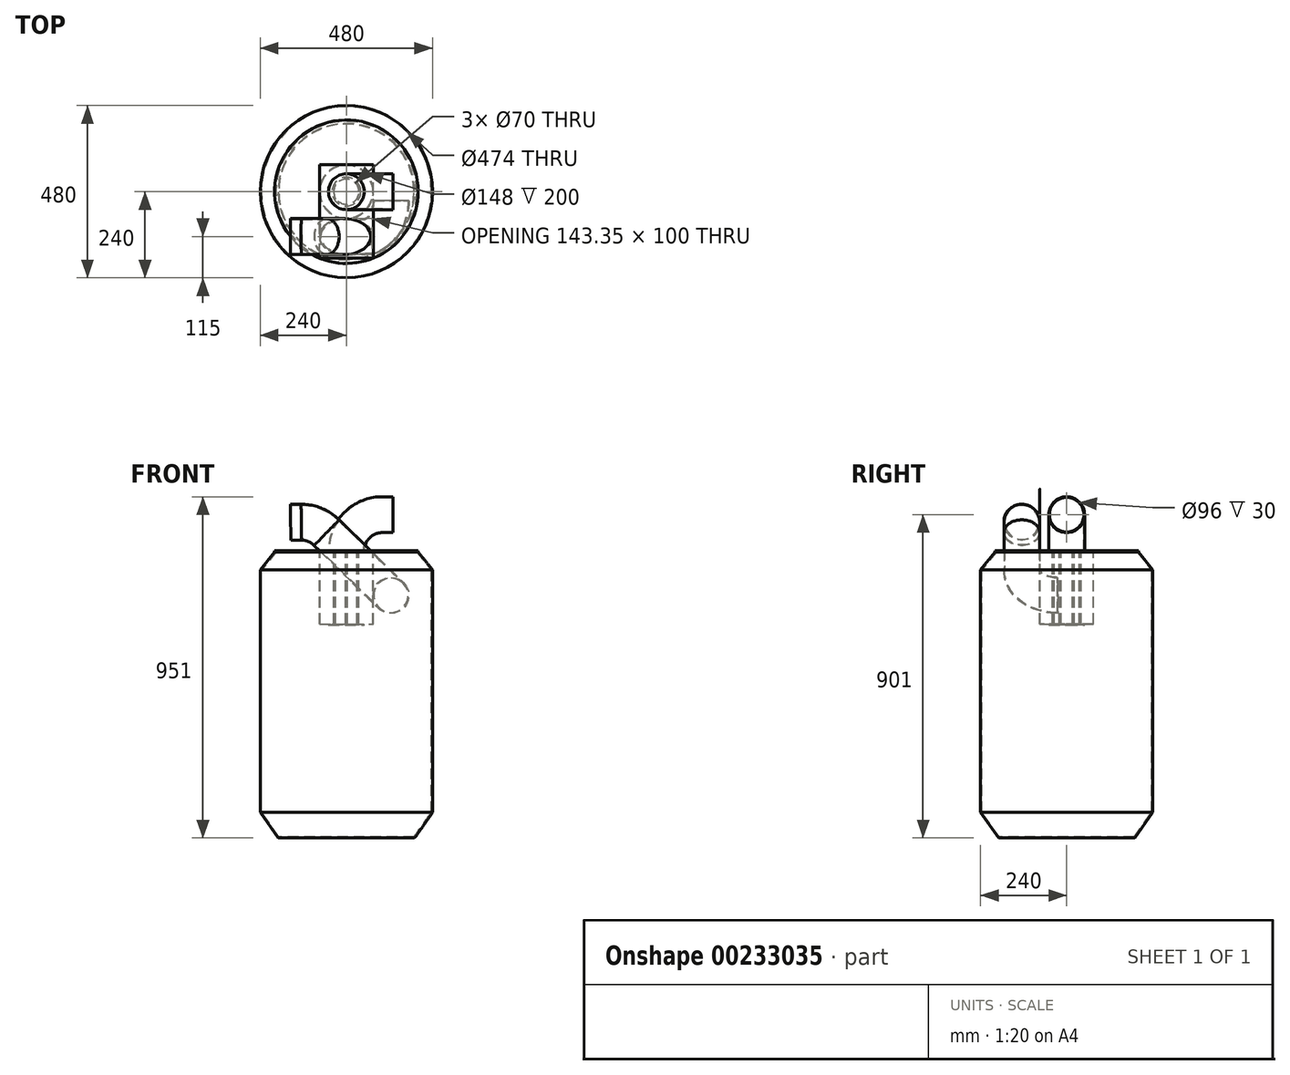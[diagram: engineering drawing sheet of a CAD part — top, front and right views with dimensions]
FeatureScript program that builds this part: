
annotation { "Feature Type Name" : "Feature", "Feature Type Description" : "" }
export const myFeature = defineFeature(function(context is Context, id is Id, definition is map)
    precondition{}
    {
        {
            assignVariable(context, id + "F0", {"name" : "FilterHeight", "anyValue" : 200});
        }
        {
            var Q0;
            Q0=qCreatedBy(makeId("Top.planeOp"),FACE);
            var sketch = newSketch(context, id + "F1", { "sketchPlane" : qUnion([Q0])});
            skCircle(sketch, "E0", {"center": v(0, 0) * mm, "radius": 200 * mm});
            skCircle(sketch, "E1", {"center": v(0, 0) * mm, "radius": 35 * mm});
            skSolve(sketch);
        }
        {
            var Q0;
            Q0=qSketchRegion(id+"F1",true);
            extrude(context, id + "F2", {"entities" : qUnion([Q0]), "depth" : 3 * mm});
        }
        {
            var Q0;
            Q0=makeQuery(id+"F2.opExtrude","CAP_FACE",FACE,{"disambiguationData":[OSD([sQuery(id+"F1.wireOp",EDGE,"E0"),sQuery(id+"F1.wireOp",EDGE,"E1")])],"isStart":true});
            var sketch = newSketch(context, id + "F3", { "sketchPlane" : qUnion([Q0])});
            skLineSegment(sketch, "E2.bottom", {"start": v(75, -75) * mm, "end": v(-75, -75) * mm});
            skLineSegment(sketch, "E2.top", {"start": v(75, 75) * mm, "end": v(-75, 75) * mm});
            skLineSegment(sketch, "E2.left", {"start": v(75, -75) * mm, "end": v(75, 75) * mm});
            skLineSegment(sketch, "E2.right", {"start": v(-75, -75) * mm, "end": v(-75, 75) * mm});
            skPoint(sketch, "E2.middle", {"position": v(0, 0) * mm});
            skCircle(sketch, "E3.0", {"center": v(0, 0) * mm, "radius": 35 * mm});
            skLineSegment(sketch, "E4.top", {"start": v(75, 185.4) * mm, "end": v(-75, 185.4) * mm});
            skLineSegment(sketch, "E4.left", {"start": v(75, 75) * mm, "end": v(75, 185.4) * mm});
            skLineSegment(sketch, "E4.right", {"start": v(-75, 75) * mm, "end": v(-75, 185.4) * mm});
            skSolve(sketch);
        }
        {
            var Q0;
            Q0=qSketchRegion(id+"F3",true);
            extrude(context, id + "F4", {"entities" : qUnion([Q0]), "depth" : 1 * mm});
        }
        {
            var Q0;
            Q0=makeQuery(id+"F4.opExtrude","CAP_FACE",FACE,{"disambiguationData":[OSD([sQuery(id+"F3.wireOp",EDGE,"E2.bottom"),sQuery(id+"F3.wireOp",EDGE,"E2.top"),sQuery(id+"F3.wireOp",EDGE,"E2.left"),sQuery(id+"F3.wireOp",EDGE,"E2.right"),sQuery(id+"F3.wireOp",EDGE,"E3.0")])],"isStart":false});
            var sketch = newSketch(context, id + "F5", { "sketchPlane" : qUnion([Q0])});
            skCircle(sketch, "E5", {"center": v(0, 37.5) * mm, "radius": 2.5 * mm});
            skCircle(sketch, "E6.1.0", {"center": v(-32.48, 18.75) * mm, "radius": 2.5 * mm});
            skCircle(sketch, "E6.2.0", {"center": v(-32.48, -18.75) * mm, "radius": 2.5 * mm});
            skCircle(sketch, "E6.3.0", {"center": v(0, -37.5) * mm, "radius": 2.5 * mm});
            skCircle(sketch, "E6.4.0", {"center": v(32.48, -18.75) * mm, "radius": 2.5 * mm});
            skCircle(sketch, "E6.5.0", {"center": v(32.48, 18.75) * mm, "radius": 2.5 * mm});
            skPoint(sketch, "E6.center", {"position": v(0, 0) * mm});
            skSolve(sketch);
        }
        {
            var Q0;
            Q0=qSketchRegion(id+"F5",true);
            extrude(context, id + "F6", {"entities" : qUnion([Q0]), "depth" : (getVariable(context, 'FilterHeight')) * mm});
        }
        {
            var Q0;
            Q0=makeQuery(id+"F6.opExtrude","CAP_FACE",FACE,{"disambiguationData":[OSD([sQuery(id+"F5.wireOp",EDGE,"E5")])],"isStart":false});
            var sketch = newSketch(context, id + "F7", { "sketchPlane" : qUnion([Q0])});
            skCircle(sketch, "E7", {"center": v(0, 0) * mm, "radius": 40 * mm});
            skSolve(sketch);
        }
        {
            var Q0;
            Q0=qSketchRegion(id+"F7",true);
            extrude(context, id + "F8", {"entities" : qUnion([Q0]), "depth" : 1 * mm});
        }
        {
            var Q0;
            Q0=makeQuery(id+"F4.opExtrude","CAP_FACE",FACE,{"disambiguationData":[OSD([sQuery(id+"F3.wireOp",EDGE,"E2.bottom"),sQuery(id+"F3.wireOp",EDGE,"E2.top"),sQuery(id+"F3.wireOp",EDGE,"E2.left"),sQuery(id+"F3.wireOp",EDGE,"E2.right"),sQuery(id+"F3.wireOp",EDGE,"E3.0")])],"isStart":false});
            var sketch = newSketch(context, id + "F9", { "sketchPlane" : qUnion([Q0])});
            skCircle(sketch, "E8", {"center": v(0, 0) * mm, "radius": 75 * mm});
            skCircle(sketch, "E9.0", {"center": v(0, 0) * mm, "radius": 74 * mm});
            skSolve(sketch);
        }
        {
            var Q0;
            Q0=qSketchRegion(id+"F9",true);
            extrude(context, id + "F10", {"entities" : qUnion([Q0]), "depth" : (getVariable(context, 'FilterHeight')) * mm});
        }
        {
            var Q0;
            Q0=makeQuery(id+"F8.opExtrude","CAP_FACE",FACE,{"disambiguationData":[OSD([sQuery(id+"F7.wireOp",EDGE,"E7")])],"isStart":false});
            var sketch = newSketch(context, id + "F11", { "sketchPlane" : qUnion([Q0])});
            skCircle(sketch, "E10", {"center": v(0, 0) * mm, "radius": 50 * mm});
            skSolve(sketch);
        }
        {
            var Q0;
            Q0=qSketchRegion(id+"F11",true);
            extrude(context, id + "F12", {"entities" : qUnion([Q0]), "depth" : 1 * mm});
        }
        {
            var Q0;
            Q0=makeQuery(id+"F2.opExtrude","CAP_FACE",FACE,{"disambiguationData":[OSD([sQuery(id+"F1.wireOp",EDGE,"E0"),sQuery(id+"F1.wireOp",EDGE,"E1")])],"isStart":false});
            var sketch = newSketch(context, id + "F13", { "sketchPlane" : qUnion([Q0])});
            skLineSegment(sketch, "E11.bottom", {"start": v(75, -75) * mm, "end": v(-75, -75) * mm});
            skLineSegment(sketch, "E11.top", {"start": v(75, 75) * mm, "end": v(-75, 75) * mm});
            skLineSegment(sketch, "E11.left", {"start": v(75, -75) * mm, "end": v(75, 75) * mm});
            skLineSegment(sketch, "E11.right", {"start": v(-75, -75) * mm, "end": v(-75, 75) * mm});
            skPoint(sketch, "E11.middle", {"position": v(0, 0) * mm});
            skCircle(sketch, "E12.0", {"center": v(0, 0) * mm, "radius": 35 * mm});
            skLineSegment(sketch, "E13.bottom", {"start": v(-75, -75) * mm, "end": v(75, -75) * mm});
            skLineSegment(sketch, "E13.top", {"start": v(-75, -185.4) * mm, "end": v(75, -185.4) * mm});
            skLineSegment(sketch, "E13.left", {"start": v(-75, -75) * mm, "end": v(-75, -185.4) * mm});
            skLineSegment(sketch, "E13.right", {"start": v(75, -75) * mm, "end": v(75, -185.4) * mm});
            skSolve(sketch);
        }
        {
            var Q0;
            Q0=qSketchRegion(id+"F13",true);
            extrude(context, id + "F14", {"entities" : qUnion([Q0]), "depth" : 1 * mm});
        }
        {
            var Q0;
            Q0=qCreatedBy(makeId("Front.planeOp"),FACE);
            var sketch = newSketch(context, id + "F15", { "sketchPlane" : qUnion([Q0])});
            skArc(sketch, "E14", {"start": v(100, 104) * mm, "mid": v(29.29, 74.71) * mm, "end": v(0, 4) * mm});
            skLineSegment(sketch, "E15", {"start": v(100, 104) * mm, "end": v(130, 104) * mm});
            skLineSegment(sketch, "E16", {"start": v(0, 4) * mm, "end": v(0, -27.41) * mm, "construction": true});
            skSolve(sketch);
        }
        {
            var Q0;
            Q0=makeQuery(id+"F14.opExtrude","CAP_FACE",FACE,{"disambiguationData":[OSD([sQuery(id+"F13.wireOp",EDGE,"E11.bottom"),sQuery(id+"F13.wireOp",EDGE,"E11.top"),sQuery(id+"F13.wireOp",EDGE,"E11.left"),sQuery(id+"F13.wireOp",EDGE,"E11.right"),sQuery(id+"F13.wireOp",EDGE,"E12.0")])],"isStart":false});
            var sketch = newSketch(context, id + "F16", { "sketchPlane" : qUnion([Q0])});
            skCircle(sketch, "E17", {"center": v(0, 0) * mm, "radius": 50 * mm});
            skCircle(sketch, "E18", {"center": v(0, 0) * mm, "radius": 48 * mm});
            skSolve(sketch);
        }
        {
            var Q0;
            Q0=makeQuery(id+"F16.imprint","IMPRINT",FACE,{"disambiguationData":[TD([[makeQuery(id+"F16.imprint","IMPRINT",EDGE,{"derivedFrom":sQuery(id+"F16.wireOp",EDGE,"E17")}),1.0]])]});
            var Q1;
            Q1=sQuery(id+"F15.wireOp",EDGE,"E14");
            var Q2;
            Q2=sQuery(id+"F15.wireOp",EDGE,"E15");
            sweep(context, id + "F17", {"profiles" : qUnion([Q0]), "path" : qUnion([Q1, Q2])});
        }
        {
            var Q0;
            Q0=makeQuery(id+"F2.opExtrude","CAP_FACE",FACE,{"disambiguationData":[OSD([sQuery(id+"F1.wireOp",EDGE,"E0"),sQuery(id+"F1.wireOp",EDGE,"E1")])],"isStart":false});
            var sketch = newSketch(context, id + "F18", { "sketchPlane" : qUnion([Q0])});
            skLineSegment(sketch, "E19", {"start": v(0, 0) * mm, "end": v(0, -207.17) * mm});
            skSolve(sketch);
        }
        {
            var Q0;
            Q0=sQuery(id+"F18.wireOp",EDGE,"E19");
            var Q1;
            Q1=makeQuery(id+"F14.opExtrude","CAP_VERTEX",VERTEX,{"disambiguationData":[OSD([sQuery(id+"F13.wireOp",EDGE,"E11.bottom"),sQuery(id+"F13.wireOp",EDGE,"E11.left")])],"isStart":false});
            cPlane(context, id + "F19", {"entities" : qUnion([Q0, Q1]), "cplaneType" : CPlaneType.LINE_ANGLE, "offset" : 25 * mm, "angle" : 45 * degree, "width" : 150 * mm, "height" : 150 * mm});
        }
        {
            var Q0;
            Q0=qCreatedBy(id+"F19.planeOp",FACE);
            var sketch = newSketch(context, id + "F20", { "sketchPlane" : qUnion([Q0])});
            skCircle(sketch, "E20", {"center": v(125, 0) * mm, "radius": 50 * mm});
            skSolve(sketch);
        }
        {
            var Q0;
            Q0=qSketchRegion(id+"F20",true);
            extrude(context, id + "F21", {"entities" : qUnion([Q0]), "operationType" : NewBodyOperationType.REMOVE, "endBound" : BoundingType.THROUGH_ALL, "oppositeDirection" : true, "depth" : 25 * mm, "hasSecondDirection" : true, "secondDirectionBound" : SecondDirectionBoundingType.THROUGH_ALL, "secondDirectionOppositeDirection" : false, "secondDirectionDepth" : 25 * mm});
        }
        {
            var Q0;
            Q0=qCreatedBy(id+"F19.planeOp",FACE);
            var sketch = newSketch(context, id + "F22", { "sketchPlane" : qUnion([Q0])});
            skCircle(sketch, "E21.0", {"center": v(125, 0) * mm, "radius": 50 * mm});
            skCircle(sketch, "E22", {"center": v(125, 0) * mm, "radius": 48 * mm});
            skSolve(sketch);
        }
        {
            var Q0;
            Q0=qSketchRegion(id+"F22",true);
            extrude(context, id + "F23", {"entities" : qUnion([Q0]), "endBound" : BoundingType.SYMMETRIC, "depth" : 150 * mm});
        }
        {
            var Q0;
            Q0=qCreatedBy(makeId("Front.planeOp"),FACE);
            cPlane(context, id + "F24", {"entities" : qUnion([Q0]), "cplaneType" : CPlaneType.OFFSET, "offset" : 125 * mm, "width" : 150 * mm, "height" : 150 * mm});
        }
        {
            var Q0;
            Q0=qCreatedBy(id+"F24.planeOp",FACE);
            var sketch = newSketch(context, id + "F25", { "sketchPlane" : qUnion([Q0])});
            skArc(sketch, "E23", {"start": v(-55.23, 53.78) * mm, "mid": v(-87.5, 75.42) * mm, "end": v(-125.59, 83.01) * mm});
            skLineSegment(sketch, "E24", {"start": v(-125.59, 83.01) * mm, "end": v(-155.59, 83.01) * mm});
            skLineSegment(sketch, "E25.0", {"start": v(-90.12, 17.96) * mm, "end": v(-20.35, 89.6) * mm, "construction": true});
            skLineSegment(sketch, "E26", {"start": v(-125.59, 83.01) * mm, "end": v(-125.59, -8.86) * mm, "construction": true});
            skSolve(sketch);
        }
        {
            var Q0;
            Q0=makeQuery(id+"F23.opExtrude","CAP_FACE",FACE,{"disambiguationData":[OSD([sQuery(id+"F22.wireOp",EDGE,"E21.0"),sQuery(id+"F22.wireOp",EDGE,"E22")])],"isStart":false});
            var sketch = newSketch(context, id + "F26", { "sketchPlane" : qUnion([Q0])});
            skCircle(sketch, "E27.0", {"center": v(125, 0) * mm, "radius": 50 * mm});
            skCircle(sketch, "E28.0", {"center": v(125, 0) * mm, "radius": 48 * mm});
            skSolve(sketch);
        }
        {
            var Q0;
            Q0=makeQuery(id+"F26.imprint","IMPRINT",FACE,{"disambiguationData":[TD([[makeQuery(id+"F26.imprint","IMPRINT",EDGE,{"derivedFrom":sQuery(id+"F26.wireOp",EDGE,"E27.0")}),1.0]])]});
            var Q1;
            Q1=sQuery(id+"F25.wireOp",EDGE,"E23");
            var Q2;
            Q2=sQuery(id+"F25.wireOp",EDGE,"E24");
            sweep(context, id + "F27", {"operationType" : NewBodyOperationType.ADD, "profiles" : qUnion([Q0]), "path" : qUnion([Q1, Q2])});
        }
        {
            var Q0;
            Q0=qCreatedBy(makeId("Right.planeOp"),FACE);
            var sketch = newSketch(context, id + "F28", { "sketchPlane" : qUnion([Q0])});
            skLineSegment(sketch, "E29", {"start": v(-200, 0) * mm, "end": v(-240, -49.57) * mm});
            skLineSegment(sketch, "E30", {"start": v(-240, -49.57) * mm, "end": v(-240, -725.99) * mm});
            skLineSegment(sketch, "E31", {"start": v(-240, -725.99) * mm, "end": v(-190, -797) * mm});
            skLineSegment(sketch, "E32", {"start": v(-190, -797) * mm, "end": v(0, -797) * mm});
            skLineSegment(sketch, "E33", {"start": v(-200, 0) * mm, "end": v(-200, 3) * mm, "construction": true});
            skLineSegment(sketch, "E34.0", {"start": v(-188.44, -794) * mm, "end": v(0, -794) * mm});
            skLineSegment(sketch, "E34.1", {"start": v(-237, -725.04) * mm, "end": v(-188.44, -794) * mm});
            skLineSegment(sketch, "E34.2", {"start": v(-237, -50.63) * mm, "end": v(-237, -725.04) * mm});
            skLineSegment(sketch, "E34.3", {"start": v(-196.15, 0) * mm, "end": v(-237, -50.63) * mm});
            skLineSegment(sketch, "E35", {"start": v(0, -797) * mm, "end": v(0, -794) * mm});
            skLineSegment(sketch, "E36", {"start": v(-196.15, 0) * mm, "end": v(-200, 0) * mm});
            skSolve(sketch);
        }
        {
            var Q0;
            Q0=qSketchRegion(id+"F28",true);
            var Q1;
            Q1=makeQuery(id+"F10.opExtrude","CAP_EDGE",EDGE,{"disambiguationData":[OSD([sQuery(id+"F9.wireOp",EDGE,"E8")])],"isStart":false});
            revolve(context, id + "F29", {"entities" : qUnion([Q0]), "axis" : qUnion([Q1]), "revolveType" : RevolveType.FULL});
        }
        {
            var Q0;
            Q0=sQuery(id+"F18.wireOp",EDGE,"E19");
            var Q1;
            Q1=makeQuery(id+"F4.opExtrude","CAP_EDGE",EDGE,{"disambiguationData":[OSD([sQuery(id+"F3.wireOp",EDGE,"E2.left"),sQuery(id+"F3.wireOp",EDGE,"E4.left")])],"isStart":true});
            cPlane(context, id + "F30", {"entities" : qUnion([Q0, Q1]), "cplaneType" : CPlaneType.LINE_ANGLE, "offset" : 25 * mm, "angle" : 318 * degree, "width" : 150 * mm, "height" : 150 * mm});
        }
        {
            var Q0;
            Q0=qCreatedBy(id+"F30.planeOp",FACE);
            var sketch = newSketch(context, id + "F31", { "sketchPlane" : qUnion([Q0])});
            skArc(sketch, "E37", {"start": v(73.08, -125) * mm, "mid": v(143.79, -95.71) * mm, "end": v(173.08, -25) * mm});
            skLineSegment(sketch, "E38", {"start": v(73.08, -125) * mm, "end": v(15.66, -125) * mm, "construction": true});
            skLineSegment(sketch, "E39", {"start": v(173.08, -25) * mm, "end": v(173.08, 19.43) * mm, "construction": true});
            skFitSpline(sketch, "E40.0", {"points": [v(72.9, -175) * mm, v(72.9, -175) * mm, v(72.9, -174.36) * mm, v(72.89, -171.5) * mm, v(72.88, -166.84) * mm, v(72.87, -160.58) * mm, v(72.87, -152.96) * mm, v(72.86, -144.26) * mm, v(72.86, -134.82) * mm, v(72.86, -125) * mm, v(72.86, -115.18) * mm, v(72.86, -105.74) * mm, v(72.87, -97.04) * mm, v(72.87, -89.42) * mm, v(72.88, -83.16) * mm, v(72.89, -78.5) * mm, v(72.9, -75.64) * mm, v(72.9, -74.68) * mm, v(72.92, -75.64) * mm, v(72.93, -78.5) * mm, v(72.93, -83.16) * mm, v(72.94, -89.42) * mm, v(72.95, -97.04) * mm, v(72.95, -105.74) * mm, v(72.95, -115.18) * mm, v(72.95, -125) * mm, v(72.95, -134.82) * mm, v(72.95, -144.26) * mm, v(72.95, -152.96) * mm, v(72.94, -160.58) * mm, v(72.93, -166.84) * mm, v(72.93, -171.5) * mm, v(72.92, -174.36) * mm, v(72.91, -175) * mm, v(72.9, -175) * mm, v(72.9, -175) * mm], "construction": true});
            skFitSpline(sketch, "E41.0", {"points": [v(72.9, -175) * mm, v(72.9, -175) * mm, v(72.9, -174.36) * mm, v(72.89, -171.5) * mm, v(72.88, -166.84) * mm, v(72.87, -160.58) * mm, v(72.87, -152.96) * mm, v(72.86, -144.26) * mm, v(72.86, -134.82) * mm, v(72.86, -125) * mm, v(72.86, -115.18) * mm, v(72.86, -105.74) * mm, v(72.87, -97.04) * mm, v(72.87, -89.42) * mm, v(72.88, -83.16) * mm, v(72.89, -78.5) * mm, v(72.9, -75.64) * mm, v(72.9, -74.68) * mm, v(72.92, -75.64) * mm, v(72.93, -78.5) * mm, v(72.93, -83.16) * mm, v(72.94, -89.42) * mm, v(72.95, -97.04) * mm, v(72.95, -105.74) * mm, v(72.95, -115.18) * mm, v(72.95, -125) * mm, v(72.95, -134.82) * mm, v(72.95, -144.26) * mm, v(72.95, -152.96) * mm, v(72.94, -160.58) * mm, v(72.93, -166.84) * mm, v(72.93, -171.5) * mm, v(72.92, -174.36) * mm, v(72.91, -175) * mm, v(72.9, -175) * mm, v(72.9, -175) * mm], "construction": true});
            skLineSegment(sketch, "E42", {"start": v(73.08, -54.23) * mm, "end": v(73.08, -228.17) * mm, "construction": true});
            skLineSegment(sketch, "E43", {"start": v(-77.1, -75) * mm, "end": v(72.9, -75) * mm, "construction": true});
            skLineSegment(sketch, "E44", {"start": v(72.9, -175) * mm, "end": v(-77.1, -175) * mm, "construction": true});
            skSolve(sketch);
        }
        {
            var Q0;
            Q0=makeQuery(id+"F23.opExtrude","CAP_FACE",FACE,{"disambiguationData":[OSD([sQuery(id+"F22.wireOp",EDGE,"E21.0"),sQuery(id+"F22.wireOp",EDGE,"E22")])],"isStart":true});
            var sketch = newSketch(context, id + "F32", { "sketchPlane" : qUnion([Q0])});
            skCircle(sketch, "E45.0", {"center": v(-125, 0) * mm, "radius": 48 * mm});
            skCircle(sketch, "E46.0", {"center": v(-125, 0) * mm, "radius": 50 * mm});
            skSolve(sketch);
        }
        {
            var Q0;
            Q0=makeQuery(id+"F32.imprint","IMPRINT",FACE,{"disambiguationData":[TD([[makeQuery(id+"F32.imprint","IMPRINT",EDGE,{"derivedFrom":sQuery(id+"F32.wireOp",EDGE,"E45.0")}),1.0]])]});
            var Q1;
            Q1=sQuery(id+"F31.wireOp",EDGE,"E37");
            sweep(context, id + "F33", {"operationType" : NewBodyOperationType.ADD, "profiles" : qUnion([Q0]), "path" : qUnion([Q1])});
        }
    });
